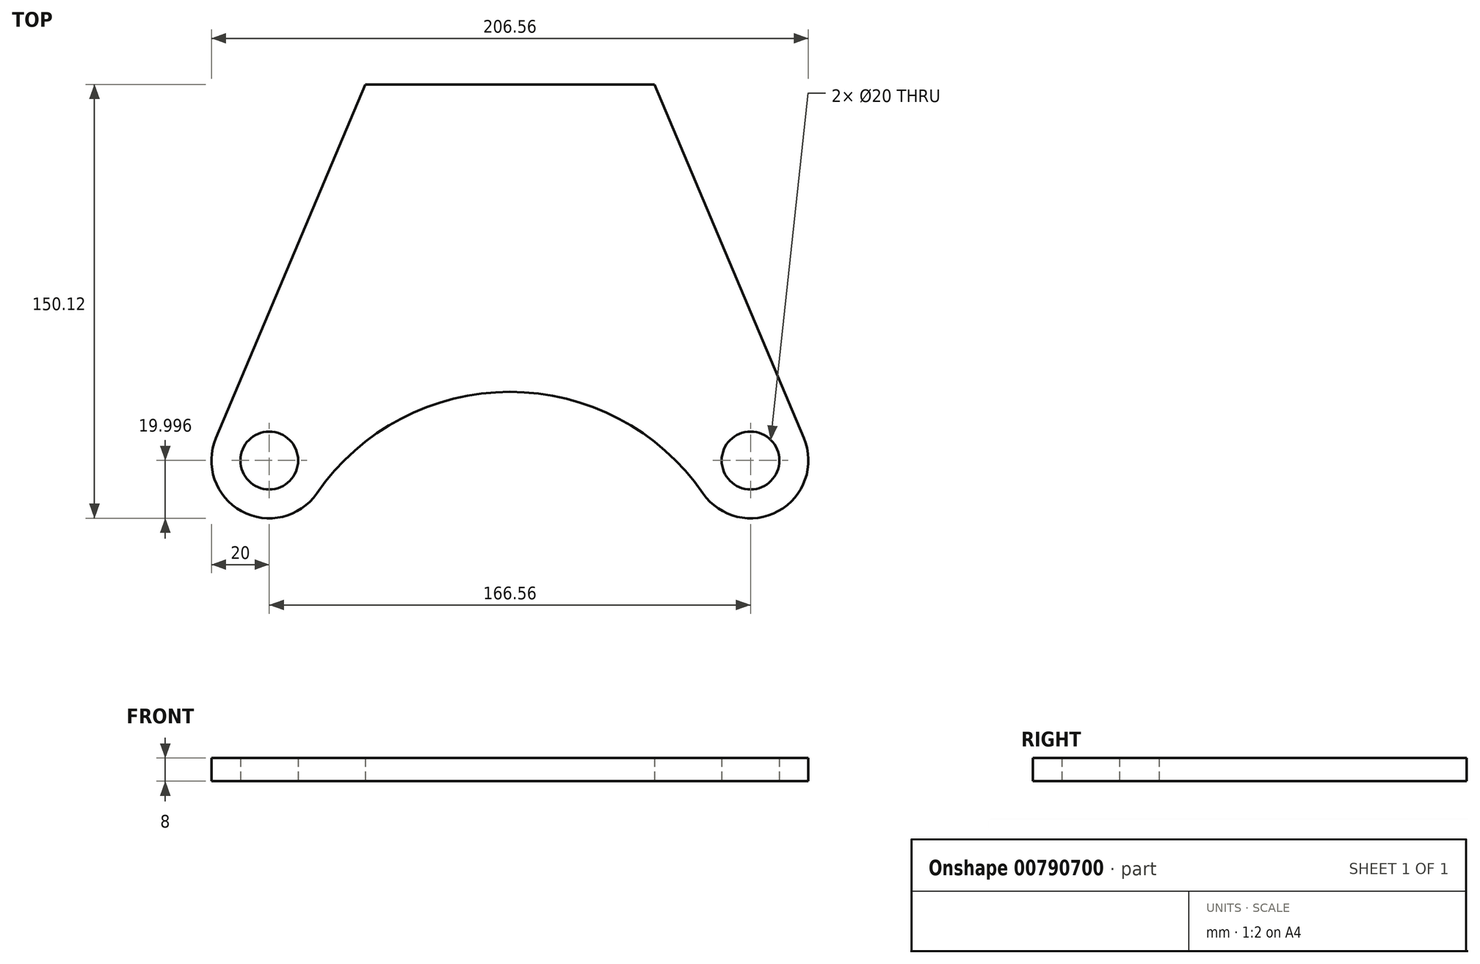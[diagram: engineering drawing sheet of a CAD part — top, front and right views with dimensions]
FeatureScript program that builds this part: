
annotation { "Feature Type Name" : "Feature", "Feature Type Description" : "" }
export const myFeature = defineFeature(function(context is Context, id is Id, definition is map)
    precondition{}
    {
        {
            var Q0;
            Q0=qCreatedBy(makeId("Top.planeOp"),FACE);
            var sketch = newSketch(context, id + "F0", { "sketchPlane" : qUnion([Q0])});
            skCircle(sketch, "E0", {"center": v(0, 0) * mm, "radius": 84 * mm});
            skCircle(sketch, "E1", {"center": v(0, -64) * mm, "radius": 20 * mm});
            skCircle(sketch, "E2.1.0", {"center": v(83.28, 80.25) * mm, "radius": 20 * mm});
            skCircle(sketch, "E2.2.0", {"center": v(-83.28, 80.25) * mm, "radius": 20 * mm});
            skPoint(sketch, "E2.center", {"position": v(0, 32.16) * mm});
            skArc(sketch, "E3", {"start": v(66.81, 68.9) * mm, "mid": v(0, 104) * mm, "end": v(-66.81, 68.9) * mm});
            skLineSegment(sketch, "E4", {"start": v(0, 210.37) * mm, "end": v(50, 210.37) * mm});
            skLineSegment(sketch, "E5", {"start": v(0, 210.37) * mm, "end": v(-50, 210.37) * mm});
            skLineSegment(sketch, "E6", {"start": v(-50, 210.37) * mm, "end": v(-101.7, 88.03) * mm});
            skLineSegment(sketch, "E7", {"start": v(50, 210.37) * mm, "end": v(101.7, 88.03) * mm});
            skCircle(sketch, "E8", {"center": v(83.28, 80.25) * mm, "radius": 10 * mm});
            skCircle(sketch, "E9", {"center": v(-83.28, 80.25) * mm, "radius": 10 * mm});
            skCircle(sketch, "E10", {"center": v(83.28, 80.25) * mm, "radius": 23.5 * mm});
            skCircle(sketch, "E11", {"center": v(-83.28, 80.25) * mm, "radius": 23.5 * mm});
            skLineSegment(sketch, "E12", {"start": v(90.84, 113.75) * mm, "end": v(-90.84, 113.75) * mm});
            skCircle(sketch, "E13", {"center": v(0, 0) * mm, "radius": 92.15 * mm});
            skSolve(sketch);
        }
        {
            var Q0;
            {var subQ0=sQuery(id+"F0.wireOp",EDGE,"E2.1.0");var subQ1=makeQuery(id+"F0.imprint","INTERSECT",VERTEX,{"derivedFrom":[subQ0,sQuery(id+"F0.wireOp",EDGE,"E3")]});Q0=makeQuery(id+"F0.imprint","IMPRINT",FACE,{"disambiguationData":[TD([[makeQuery(id+"F0.imprint","IMPRINT",EDGE,{"disambiguationData":[TD([[subQ1,-1.0]])],"derivedFrom":subQ0}),1.0]])]});}
            var Q1;
            {var subQ0=sQuery(id+"F0.wireOp",EDGE,"E3");Q1=makeQuery(id+"F0.imprint","IMPRINT",FACE,{"disambiguationData":[TD([[makeQuery(id+"F0.imprint","IMPRINT",EDGE,{"derivedFrom":subQ0}),-1.0]])]});}
            var Q2;
            {var subQ0=sQuery(id+"F0.wireOp",EDGE,"E2.2.0");var subQ1=makeQuery(id+"F0.imprint","IMPRINT",VERTEX,{"derivedFrom":subQ0});Q2=makeQuery(id+"F0.imprint","IMPRINT",FACE,{"disambiguationData":[TD([[makeQuery(id+"F0.imprint","IMPRINT",EDGE,{"disambiguationData":[TD([[subQ1,-1.0]])],"derivedFrom":subQ0}),1.0]])]});}
            var Q3;
            {var subQ0=sQuery(id+"F0.wireOp",EDGE,"E2.2.0");var subQ1=makeQuery(id+"F0.imprint","INTERSECT",VERTEX,{"derivedFrom":[subQ0,sQuery(id+"F0.wireOp",EDGE,"E3")]});Q3=makeQuery(id+"F0.imprint","IMPRINT",FACE,{"disambiguationData":[TD([[makeQuery(id+"F0.imprint","IMPRINT",EDGE,{"disambiguationData":[TD([[subQ1,1.0]])],"derivedFrom":subQ0}),1.0]])]});}
            var Q4;
            {var subQ4=sQuery(id+"F0.wireOp",EDGE,"E4");Q4=makeQuery(id+"F0.imprint","IMPRINT",FACE,{"disambiguationData":[TD([[makeQuery(id+"F0.imprint","IMPRINT",EDGE,{"derivedFrom":subQ4}),-1.0]])]});}
            var Q5;
            {var subQ5=sQuery(id+"F0.wireOp",EDGE,"E12");Q5=makeQuery(id+"F0.imprint","IMPRINT",FACE,{"disambiguationData":[TD([[makeQuery(id+"F0.imprint","IMPRINT",EDGE,{"derivedFrom":subQ5}),1.0]])]});}
            extrude(context, id + "F1", {"entities" : qUnion([Q0, Q1, Q2, Q3, Q4, Q5]), "depth" : 8 * mm, "offsetDistance" : 25 * mm});
        }
    });
